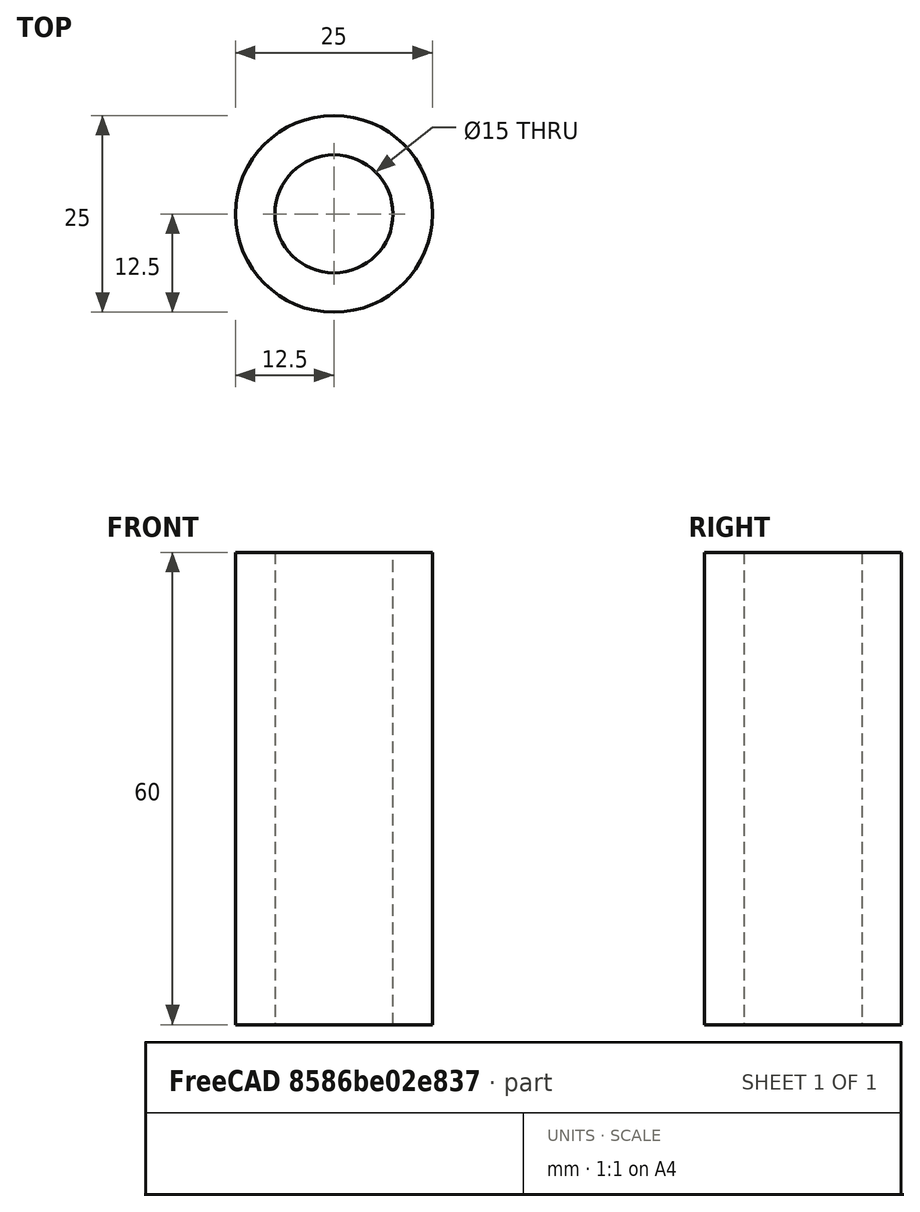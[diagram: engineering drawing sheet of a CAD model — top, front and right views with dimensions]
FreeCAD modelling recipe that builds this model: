
FCSTD DOCUMENT  (FreeCAD 0.21R33771 (Git))
Label: bushing
License: All rights reserved
LicenseURL: https://en.wikipedia.org/wiki/All_rights_reserved
objects: Sketcher::SketchObject×1, PartDesign::Pad×1, PartDesign::Body×1, App::Part×1, Spreadsheet::Sheet×1
note: 4 computed .brp shape members not serialized (recipe doc carries the construction recipe); baked Part::Feature solids carry a one-line shape summary decoded from their .brp

FEATURE [Sketcher::SketchObject] Sketch
  FullyConstrained = true
  MapMode = 5
  Support = -> [XY_Plane001]
  sketch-geometry (2):
    g0: Circle CenterX=0 CenterY=0 CenterZ=0 NormalX=0 NormalY=0 NormalZ=1 AngleXU=0 Radius=12.5
    g1: Circle CenterX=0 CenterY=0 CenterZ=0 NormalX=0 NormalY=0 NormalZ=1 AngleXU=0 Radius=7.5
  constraints (4):
    c: Coincident(g0,g-1)
    c: Coincident(g1,g0)
    c: Diameter(g0) = 25
    c: Diameter(g1) = 15
FEATURE [PartDesign::Pad] Pad
  Direction = (0,0,1)
  Length = 60
  Length2 = 10
  Profile = -> Sketch
  ReferenceAxis = -> Sketch [N_Axis]
  Type = 0
FEATURE [PartDesign::Body] Body
  Group = -> [Sketch,Pad]
  Origin = -> Origin001
  Tip = -> Pad
FEATURE [App::Part] Part
  Group = -> [Body]
  Origin = -> Origin
FEATURE [Spreadsheet::Sheet] bushing_data
  cells = A1='Information of element; A2='________________________; A3='28/08/2024 04:00:27; A4='Document name; B4='Unnamed; A5='Label of the object; B5='Body; A6='Internal name of the object; B6='Body; A7='Element name; A8='Object Type (Shape); B8='Solid; A9='Object Type; B9='Part::TopoShape; A10='Mouse coordinates; B10='X; C10=0; D10='mm; E10='Y; F10=0; G10='mm; H10='Z; I10=0; J10='mm; A11='Color on selection; A12='Red; B12=0; C12='Green; D12=0; E12='Blue; F12=0; G12='Transparency; H12=0; A13='Object Color (float) ; B13='Red; C13=0.800000011920929; D13='Green; E13=0.800000011920929; F13='Blue; G13=0.800000011920929; H13='Transparency; I13=0; A14='Object Color (int  ) ; B14='Red; C14=204; D14='Green; E14=204; F14='Blue; G14=204; H14='Transparency; I14=0; A15='Object Color (float) ; B15='Red; C15=0.0980392172932625; D15='Green; E15=0.0980392172932625; F15='Blue; G15=0.0980392172932625; H15='Transparency; I15=0; A16='Color Line(s) (int  ) ; B16='Red; C16=25; D16='Green; E16=25; F16='Blue; G16=25; H16='Transparency; I16=0; A17='Color Point(s) (float) ; B17='Red; C17=0.0980392172932625; D17='Green; E17=0.0980392172932625; F17='Blue; G17=0.0980392172932625; H17='Transparency; I17=0; A18='Color Point(s) (int  ) ; B18='Red; C18=25; D18='Green; E18=25; F18='Blue; G18=25; H18='Transparency; I18=0; A19='Length of the object; B19=0; C19='mm; A20='Shape Perimeter; B20=371.3274; C20='mm; A22='Plane; B22=' XY:; C22==0 deg; D22=' coordinates:; E22='[,0.0 , 0.0,]  [,0.0 , 0.0,]; A23='Plane; B23=' YZ:; C23==0 deg; D23=' coordinates:; E23='[,0.0 , 0.0,]  [,0.0 , 0.0,]; A24='Plane; B24=' ZX:; C24==0 deg; D24=' coordinates:; E24='[,0.0 , 0.0,]  [,0.0 , 0.0,]; A25='Shape area; B25=8168.1409; C25='mm2; A26='Face area; B26=0; C26='mm2; A27='Volume of the form; B27=18849.5559; C27='mm3; A28='Mass; B28=199.9938; C28='g; D28=' Density:; E28=10.61; A29='Shape center; B29=' X:; C29=0; D29='mm; E29=' Y:; F29=0; G29='mm; H29=' Z:; I29=30; J29='mm; A30='Center of mass; B30=' X:; C30=0; D30='mm; E30=' Y:; F30=-0; G30='mm; H30=' Z:; I30=30; J30='mm; A31='Overall dimensions; B31=' X:; C31=25; D31='mm; E31=' Y:; F31=24.9301; G31='mm; H31=' Z:; I31=60; J31='mm; A32='Diagonal dimensions; B32=69.6169; C32='mm; A33='Direction; B33=' X:; C33=0; D33=' Y:; E33=0; F33=' Z:; G33=60; A35='Matrix of inertia; B35='mm^5; A36=' X:; B36=6656249.4348; C36=' Y:; D36=0; E36=' Z:; F36=-0; G36=' :; H36=0; A37=' X:; B37=0; C37=' Y:; D37=6656249.4348; E37=' Z:; F37=0; G37=' :; H37=0; A38=' X:; B38=-0; C38=' Y:; D38=0; E38=' Z:; F38=2002765.3167; G38=' :; H38=0; A39=' X:; B39=0; C39=' Y:; D39=0; E39=' Z:; F39=0; G39=' :; H39=1; A40='Matrix inertia massique; B40='gmm2; A41=' X:; B41=70622.8065; +1240 more cells
